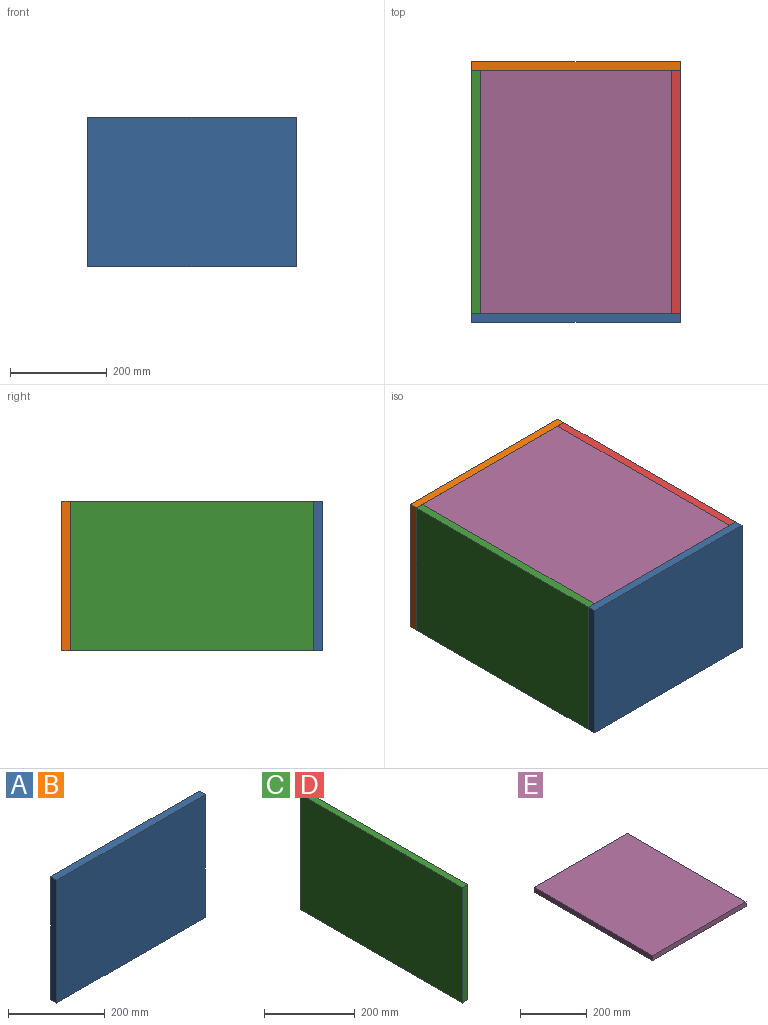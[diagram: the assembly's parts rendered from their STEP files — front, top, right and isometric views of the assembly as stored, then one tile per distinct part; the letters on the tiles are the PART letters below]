
ASSEMBLY  parts=5 mates=12
PART A: 6 faces, bbox 433x18x310 mm
  f0: plane 310x18mm, normal (-1,0,0), area 5580mm2, adj f1,f3,f4,f5
  f1: plane 433x18mm, normal (0,0,-1), area 7794mm2, adj f0,f2,f4,f5
  f2: plane 310x18mm, normal (1,0,0), area 5580mm2, adj f1,f3,f4,f5
  f3: plane 433x18mm, normal (0,0,1), area 7794mm2, adj f0,f2,f4,f5
  f4: plane 433x310mm, normal (0,-1,0), area 134230mm2, adj f0,f1,f2,f3
  f5: plane 433x310mm, normal (0,1,0), area 134230mm2, adj f0,f1,f2,f3
PART B: same geometry as A
PART C: 6 faces, bbox 18x504x310 mm
  f0: plane 310x18mm, normal (0,-1,0), area 5580mm2, adj f1,f3,f4,f5
  f1: plane 504x18mm, normal (0,0,-1), area 9072mm2, adj f0,f2,f4,f5
  f2: plane 310x18mm, normal (0,1,0), area 5580mm2, adj f1,f3,f4,f5
  f3: plane 504x18mm, normal (0,0,1), area 9072mm2, adj f0,f2,f4,f5
  f4: plane 504x310mm, normal (1,0,0), area 156240mm2, adj f0,f1,f2,f3
  f5: plane 504x310mm, normal (-1,0,0), area 156240mm2, adj f0,f1,f2,f3
PART D: same geometry as C
PART E: 6 faces, bbox 397x504x18 mm
  f0: plane 504x18mm, normal (-1,0,0), area 9072mm2, adj f1,f3,f4,f5
  f1: plane 397x18mm, normal (0,-1,0), area 7146mm2, adj f0,f2,f4,f5
  f2: plane 504x18mm, normal (1,0,0), area 9072mm2, adj f1,f3,f4,f5
  f3: plane 397x18mm, normal (0,1,0), area 7146mm2, adj f0,f2,f4,f5
  f4: plane 504x397mm, normal (0,0,1), area 200088mm2, adj f0,f1,f2,f3
  f5: plane 504x397mm, normal (0,0,-1), area 200088mm2, adj f0,f1,f2,f3
PLACE A rot(axis=(1,0,0),180deg) t=(-42.32,-328.42,-169.09)mm
PLACE B rot(axis=(1,0,0),180deg) t=(-42.32,193.58,-169.09)mm
PLACE C t=(-42.32,-310.42,-479.09)mm
PLACE D t=(372.68,-310.42,-479.09)mm
PLACE E rot(axis=(0,1,0),180deg) t=(372.68,-310.42,-169.09)mm
MATE planar B.f5 <-> E.f3  axis (0,-1,0) through (174.18,193.58,-324.09)mm
MATE planar C.f0 <-> A.f4  axis (0,-1,0) through (-33.32,-310.42,-324.09)mm
MATE planar B.f1 <-> E.f5  axis (0,0,1) through (174.18,202.58,-169.09)mm
MATE planar C.f3 <-> E.f5  axis (0,0,1) through (-33.32,-58.42,-169.09)mm
MATE planar A.f1 <-> E.f5  axis (0,0,1) through (174.18,-319.42,-169.09)mm
MATE planar D.f5 <-> E.f0  axis (-1,0,0) through (372.68,-58.42,-324.09)mm
MATE planar A.f0 <-> C.f5  axis (-1,0,0) through (-42.32,-319.42,-324.09)mm
MATE planar A.f4 <-> E.f1  axis (0,1,0) through (174.18,-310.42,-324.09)mm
MATE planar D.f3 <-> E.f5  axis (0,0,1) through (381.68,-58.42,-169.09)mm
MATE planar C.f4 <-> E.f2  axis (1,0,0) through (-24.32,-58.42,-324.09)mm
MATE planar D.f2 <-> B.f5  axis (0,1,0) through (381.68,193.58,-324.09)mm
MATE planar B.f0 <-> C.f5  axis (-1,0,0) through (-42.32,202.58,-324.09)mm
